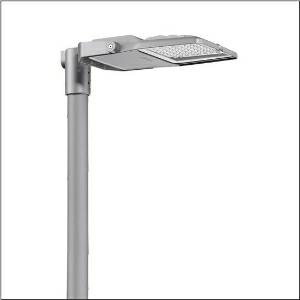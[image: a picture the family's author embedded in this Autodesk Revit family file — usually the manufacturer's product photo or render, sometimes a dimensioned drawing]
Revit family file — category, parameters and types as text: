
# Revit family: floodlight_fl_21_iq_mini___pl61_5xa7771b4c3a_e6c4
name_source: partatom
category: Lighting Fixtures
units: mm (PartAtom-declared; Revit-internal decimal feet)

## family parameters
Cut with Voids When Loaded = No
Host = Face
Light Source = No
Part Type = Normal
Room Calculation Point = No
Round Connector Dimension = Use Diameter
Shared = No

## types (1)
- --- (1 x LED, 6370 lm, 45.5 W, 4000K)
    Apparent Load = 46 VA
    CIE Flux Codes = 33 65 98 100 100
    Color Rendering = 70
    Color Temperature = 4000K
    Default Elevation = 1800 mm
    Description = Floodlight FL 21 iQ mini, floodlight, primary light control with lens, of PMMA, primary optical cover: protective disc, of toughened safety glass, transparent, light distribution: PL61, light emission: direct distribution, installation type: surface-mounted, LED, High Power LED, rated luminous flux: 6.370lm, luminous efficacy: 140lm/W, light colour: 740, colour temperature: 4000K, control gear: iQ Comfort/DALI, control: Auto-Match, Temp-Guard, Lumen-Switch, Night-Set, Smart-Wire, Light-Fading, Desk-Remote (wireless, voltage-free reading and setting of iQ features in the workshop via application-optimized NFC function/RFID function), optimised constant luminous flux control (CLO 2.0), with terminal, 6-pole, mains connection: 220..240V, AC, 50/60Hz, start of lifetime: 46W, end of service life: 48W, reduction: 22W, luminaire housing, of diecast aluminium, powder-coated, Siteco® metallic grey (DB 702S), corrosivity category C5 mid according to DIN EN ISO 12944, suitable for swimming pools, chlorine-resistant, sealing non-destructively replaceable, please order mast flange separately, mast bracket, of steel, galvanised, powder-coated, Siteco® metallic grey (DB 702S), protection rating (complete): IP66, insulation class (complete): insulation class II (safety insulation), certification: CE, ENEC, VDE, protection symbol: D, impact resistance: IK08, permissible operating ambient temperature: -40..+40°C, permissible operating ambient temperature for outdoor applications: -40..+50°C, standard: DIN EN 12944, LABS conformity tested according to VDMA 24364:2018-05, packaging unit: 1 piece

Light Distribution: PL61
    Height = 70 mm
    Lamp = 1 x LED
    Lamp Light Flux = 6370 lm
    Lamp Power = 45.5 W
    Lamp count = 1
    Length = 485 mm
    Luminous efficacy = 140 lm/W
    Manufacturer = Siteco
    ModVariant = No
    Model = 5XA7771B4C3A
    Number of Poles = 1
    OnlyDefault = Yes
    Power Factor = 1
    Product Name = Floodlight FL 21 iQ mini | PL61
    Product group = floodlight | pylon annexe
    ProductGroupID = 6201
    Protection Class = Protection class II
    Protection Degree = IP 66
    RLX_Detail_Level = 1
    RLX_Emergency_Light_Flux = 0 lm
    RLX_Emergency_Type = 0
    RLX_Emergency_Type_DB = No
    RlxData = <blob elided: 101437 chars, md5=82e26c74>
    Socket = socket
    Standby Power = 0 W
    System Light Flux = 6370 lm
    System Power = 46 W
    Type Comments = factory setting: luminous flux: 100 % | dim-lin: 254 | 463 mA
    Type Image = l_1007125.jpg
    URL = http://relux.com
    VarID = @adj_195201
    Voltage = 0 V
    Weight = 0.00 kg
    Width = 337 mm

## geometry (parser evidence)
native form markers: Blend x4, Sweep x13
no freeform markers — native parametric forms only
